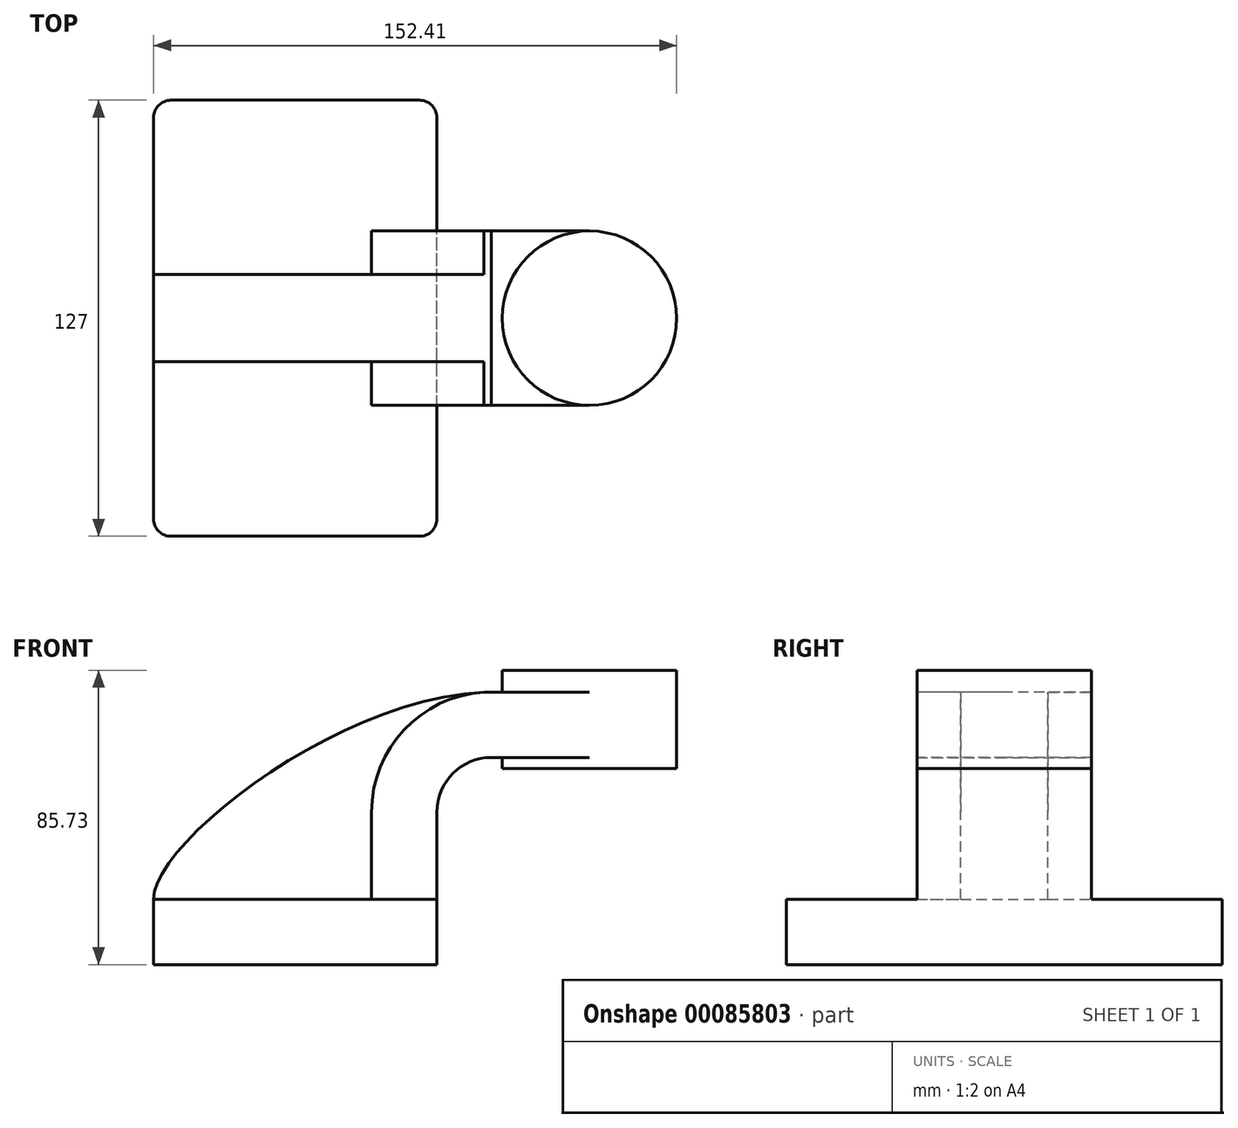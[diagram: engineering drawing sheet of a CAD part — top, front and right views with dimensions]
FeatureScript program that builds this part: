
annotation { "Feature Type Name" : "Feature", "Feature Type Description" : "" }
export const myFeature = defineFeature(function(context is Context, id is Id, definition is map)
    precondition{}
    {
        {
            var Q0;
            Q0=qCreatedBy(makeId("Front.planeOp"),FACE);
            var sketch = newSketch(context, id + "F0", { "sketchPlane" : qUnion([Q0])});
            skLineSegment(sketch, "E0.bottom", {"start": v(-41.28, 9.52) * mm, "end": v(41.27, 9.53) * mm});
            skLineSegment(sketch, "E0.top", {"start": v(-41.28, -9.53) * mm, "end": v(41.28, -9.53) * mm});
            skLineSegment(sketch, "E0.left", {"start": v(-41.28, 9.52) * mm, "end": v(-41.27, -9.53) * mm});
            skLineSegment(sketch, "E0.right", {"start": v(41.28, 9.53) * mm, "end": v(41.28, -9.52) * mm});
            skPoint(sketch, "E0.middle", {"position": v(0, 0) * mm});
            skLineSegment(sketch, "E1.bottom", {"start": v(60.32, 47.63) * mm, "end": v(111.12, 47.63) * mm});
            skLineSegment(sketch, "E1.top", {"start": v(60.32, 76.2) * mm, "end": v(111.12, 76.2) * mm});
            skLineSegment(sketch, "E1.left", {"start": v(60.32, 47.63) * mm, "end": v(60.32, 76.2) * mm});
            skLineSegment(sketch, "E1.right", {"start": v(111.12, 47.63) * mm, "end": v(111.12, 76.2) * mm});
            skPoint(sketch, "E1.middle", {"position": v(85.72, 61.91) * mm});
            skLineSegment(sketch, "E2", {"start": v(41.27, 9.53) * mm, "end": v(41.27, 34.93) * mm});
            skArc(sketch, "E3", {"start": v(41.27, 34.93) * mm, "mid": v(45.92, 46.15) * mm, "end": v(57.15, 50.8) * mm});
            skLineSegment(sketch, "E4", {"start": v(57.15, 50.8) * mm, "end": v(73.75, 50.8) * mm});
            skLineSegment(sketch, "E5.0", {"start": v(57.15, 69.85) * mm, "end": v(73.75, 69.85) * mm});
            skArc(sketch, "E5.1", {"start": v(22.23, 34.93) * mm, "mid": v(32.45, 59.62) * mm, "end": v(57.15, 69.85) * mm});
            skLineSegment(sketch, "E5.2", {"start": v(22.22, 9.53) * mm, "end": v(22.22, 34.93) * mm});
            skLineSegment(sketch, "E6", {"start": v(73.75, 69.85) * mm, "end": v(85.72, 69.85) * mm});
            skLineSegment(sketch, "E7", {"start": v(85.72, 69.85) * mm, "end": v(85.72, 61.91) * mm});
            skLineSegment(sketch, "E8", {"start": v(73.75, 50.8) * mm, "end": v(85.72, 50.8) * mm});
            skPoint(sketch, "E8.endSnap0", {"position": v(85.72, 47.63) * mm});
            skLineSegment(sketch, "E9", {"start": v(85.72, 50.8) * mm, "end": v(85.72, 61.91) * mm});
            skFitSpline(sketch, "E10", {"points": [v(-41.27, 9.52) * mm, v(57.15, 69.85) * mm], "startDerivative": vector(-0.57, 49.26) * mm, "endDerivative": vector(131.94, 2.1) * mm});
            skLineSegment(sketch, "E11", {"start": v(85.72, 47.63) * mm, "end": v(85.72, 76.2) * mm});
            skSolve(sketch);
        }
        {
            var Q0;
            Q0=makeQuery(id+"F0.imprint","IMPRINT",FACE,{"disambiguationData":[TD([[makeQuery(id+"F0.imprint","IMPRINT",EDGE,{"derivedFrom":sQuery(id+"F0.wireOp",EDGE,"E0.top")}),1.0]])]});
            extrude(context, id + "F1", {"entities" : qUnion([Q0]), "endBound" : BoundingType.SYMMETRIC, "depth" : 127 * mm});
        }
        {
            var Q0;
            {var subQ1=sQuery(id+"F0.wireOp",EDGE,"E2");Q0=makeQuery(id+"F0.imprint","IMPRINT",FACE,{"disambiguationData":[TD([[makeQuery(id+"F0.imprint","IMPRINT",EDGE,{"derivedFrom":subQ1}),1.0]])]});}
            var Q1;
            {var subQ0=sQuery(id+"F0.wireOp",EDGE,"E6");Q1=makeQuery(id+"F0.imprint","IMPRINT",FACE,{"disambiguationData":[TD([[makeQuery(id+"F0.imprint","IMPRINT",EDGE,{"derivedFrom":subQ0}),-1.0]])]});}
            extrude(context, id + "F2", {"entities" : qUnion([Q0, Q1]), "operationType" : NewBodyOperationType.ADD, "endBound" : BoundingType.SYMMETRIC, "depth" : 50.8 * mm});
        }
        {
            var Q0;
            {var subQ3=sQuery(id+"F0.wireOp",EDGE,"E5.2");Q0=makeQuery(id+"F0.imprint","IMPRINT",FACE,{"disambiguationData":[TD([[makeQuery(id+"F0.imprint","IMPRINT",EDGE,{"derivedFrom":subQ3}),1.0]])]});}
            extrude(context, id + "F3", {"entities" : qUnion([Q0]), "operationType" : NewBodyOperationType.ADD, "endBound" : BoundingType.SYMMETRIC, "depth" : 25.4 * mm});
        }
        {
            var Q0;
            {var subQ0=sQuery(id+"F0.wireOp",EDGE,"E1.right");Q0=makeQuery(id+"F0.imprint","IMPRINT",FACE,{"disambiguationData":[TD([[makeQuery(id+"F0.imprint","IMPRINT",EDGE,{"derivedFrom":subQ0}),1.0]])]});}
            var Q1;
            Q1=sQuery(id+"F0.wireOp",EDGE,"E11");
            revolve(context, id + "F4", {"operationType" : NewBodyOperationType.ADD, "entities" : qUnion([Q0]), "axis" : qUnion([Q1]), "revolveType" : RevolveType.FULL});
        }
        {
            var Q0;
            Q0=makeQuery(id+"F1.opExtrude","CAP_EDGE",EDGE,{"disambiguationData":[OSD([sQuery(id+"F0.wireOp",EDGE,"E0.left")])],"isStart":false});
            var Q1;
            Q1=makeQuery(id+"F1.opExtrude","CAP_EDGE",EDGE,{"disambiguationData":[OSD([sQuery(id+"F0.wireOp",EDGE,"E0.right")])],"isStart":false});
            var Q2;
            Q2=makeQuery(id+"F1.opExtrude","CAP_EDGE",EDGE,{"disambiguationData":[OSD([sQuery(id+"F0.wireOp",EDGE,"E0.right")])],"isStart":true});
            var Q3;
            Q3=makeQuery(id+"F1.opExtrude","CAP_EDGE",EDGE,{"disambiguationData":[OSD([sQuery(id+"F0.wireOp",EDGE,"E0.left")])],"isStart":true});
            fillet(context, id + "F5", {"entities" : qUnion([Q0, Q1, Q2, Q3]), "radius" : 5.08 * mm, "tangentPropagation" : true, "allowEdgeOverflow" : false});
        }
    });
